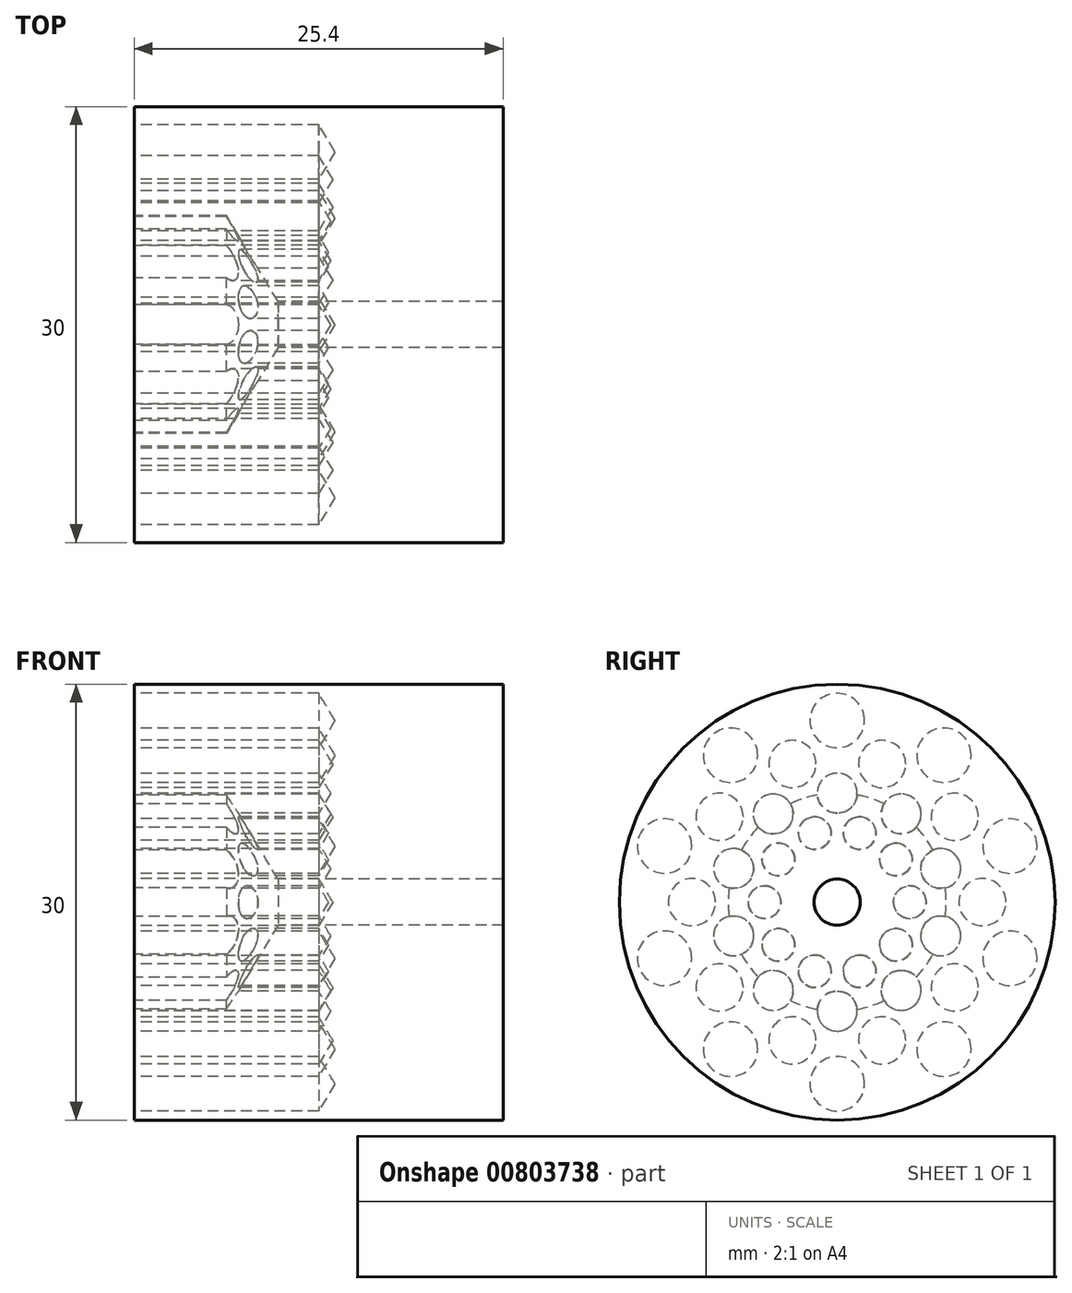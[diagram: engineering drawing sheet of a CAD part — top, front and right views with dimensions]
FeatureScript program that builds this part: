
annotation { "Feature Type Name" : "Feature", "Feature Type Description" : "" }
export const myFeature = defineFeature(function(context is Context, id is Id, definition is map)
    precondition{}
    {
        {
            var Q0;
            Q0=qCreatedBy(makeId("Right.planeOp"),FACE);
            var sketch = newSketch(context, id + "F0", { "sketchPlane" : qUnion([Q0])});
            skCircle(sketch, "E0", {"center": v(0, 0) * mm, "radius": 15 * mm});
            skCircle(sketch, "E1", {"center": v(0, 0) * mm, "radius": 1.59 * mm});
            skSolve(sketch);
        }
        {
            var Q0;
            Q0=makeQuery(id+"F0.imprint","IMPRINT",FACE,{"disambiguationData":[TD([[makeQuery(id+"F0.imprint","IMPRINT",EDGE,{"derivedFrom":sQuery(id+"F0.wireOp",EDGE,"E0")}),1.0]])]});
            extrude(context, id + "F1", {"entities" : qUnion([Q0]), "depth" : 25.4 * mm, "offsetDistance" : 25.4 * mm});
        }
        {
            var Q0;
            Q0=makeQuery(id+"F1.opExtrude","CAP_FACE",FACE,{"disambiguationData":[OSD([sQuery(id+"F0.wireOp",EDGE,"E0"),sQuery(id+"F0.wireOp",EDGE,"E1")])],"isStart":true});
            var sketch = newSketch(context, id + "F2", { "sketchPlane" : qUnion([Q0])});
            skCircle(sketch, "E2.cCircle", {"center": v(0, 0) * mm, "radius": 12.5 * mm, "construction": true});
            skLineSegment(sketch, "E2.0", {"start": v(0, 12.5) * mm, "end": v(7.35, 10.11) * mm});
            skLineSegment(sketch, "E2.1", {"start": v(7.35, 10.11) * mm, "end": v(11.89, 3.86) * mm});
            skLineSegment(sketch, "E2.2", {"start": v(11.89, 3.86) * mm, "end": v(11.89, -3.86) * mm});
            skLineSegment(sketch, "E2.3", {"start": v(11.89, -3.86) * mm, "end": v(7.35, -10.11) * mm});
            skLineSegment(sketch, "E2.4", {"start": v(7.35, -10.11) * mm, "end": v(0, -12.5) * mm});
            skLineSegment(sketch, "E2.5", {"start": v(0, -12.5) * mm, "end": v(-7.35, -10.11) * mm});
            skLineSegment(sketch, "E2.6", {"start": v(-7.35, -10.11) * mm, "end": v(-11.89, -3.86) * mm});
            skLineSegment(sketch, "E2.7", {"start": v(-11.89, -3.86) * mm, "end": v(-11.89, 3.86) * mm});
            skLineSegment(sketch, "E2.8", {"start": v(-11.89, 3.86) * mm, "end": v(-7.35, 10.11) * mm});
            skLineSegment(sketch, "E2.9", {"start": v(-7.35, 10.11) * mm, "end": v(0, 12.5) * mm});
            skCircle(sketch, "E3.cCircle", {"center": v(0, 0) * mm, "radius": 10 * mm, "construction": true});
            skLineSegment(sketch, "E3.0", {"start": v(-10, 0) * mm, "end": v(-8.1, 5.88) * mm});
            skLineSegment(sketch, "E3.1", {"start": v(-8.1, 5.88) * mm, "end": v(-3.1, 9.51) * mm});
            skLineSegment(sketch, "E3.2", {"start": v(-3.1, 9.51) * mm, "end": v(3.1, 9.51) * mm});
            skLineSegment(sketch, "E3.3", {"start": v(3.1, 9.51) * mm, "end": v(8.1, 5.88) * mm});
            skLineSegment(sketch, "E3.4", {"start": v(8.1, 5.88) * mm, "end": v(10, 0) * mm});
            skLineSegment(sketch, "E3.5", {"start": v(10, 0) * mm, "end": v(8.1, -5.88) * mm});
            skLineSegment(sketch, "E3.6", {"start": v(8.1, -5.88) * mm, "end": v(3.1, -9.51) * mm});
            skLineSegment(sketch, "E3.7", {"start": v(3.1, -9.51) * mm, "end": v(-3.1, -9.51) * mm});
            skLineSegment(sketch, "E3.8", {"start": v(-3.1, -9.51) * mm, "end": v(-8.1, -5.88) * mm});
            skLineSegment(sketch, "E3.9", {"start": v(-8.1, -5.88) * mm, "end": v(-10, 0) * mm});
            skCircle(sketch, "E4.cCircle", {"center": v(0, 0) * mm, "radius": 7.5 * mm, "construction": true});
            skLineSegment(sketch, "E4.0", {"start": v(0, 7.5) * mm, "end": v(4.4, 6.07) * mm});
            skLineSegment(sketch, "E4.1", {"start": v(4.4, 6.07) * mm, "end": v(7.13, 2.32) * mm});
            skLineSegment(sketch, "E4.2", {"start": v(7.13, 2.32) * mm, "end": v(7.13, -2.32) * mm});
            skLineSegment(sketch, "E4.3", {"start": v(7.13, -2.32) * mm, "end": v(4.4, -6.07) * mm});
            skLineSegment(sketch, "E4.4", {"start": v(4.4, -6.07) * mm, "end": v(0, -7.5) * mm});
            skLineSegment(sketch, "E4.5", {"start": v(0, -7.5) * mm, "end": v(-4.4, -6.07) * mm});
            skLineSegment(sketch, "E4.6", {"start": v(-4.4, -6.07) * mm, "end": v(-7.13, -2.32) * mm});
            skLineSegment(sketch, "E4.7", {"start": v(-7.13, -2.32) * mm, "end": v(-7.13, 2.32) * mm});
            skLineSegment(sketch, "E4.8", {"start": v(-7.13, 2.32) * mm, "end": v(-4.4, 6.07) * mm});
            skLineSegment(sketch, "E4.9", {"start": v(-4.4, 6.07) * mm, "end": v(0, 7.5) * mm});
            skCircle(sketch, "E5.cCircle", {"center": v(0, 0) * mm, "radius": 5 * mm, "construction": true});
            skLineSegment(sketch, "E5.0", {"start": v(-5, 0) * mm, "end": v(-4.05, 2.94) * mm});
            skLineSegment(sketch, "E5.1", {"start": v(-4.05, 2.94) * mm, "end": v(-1.55, 4.76) * mm});
            skLineSegment(sketch, "E5.2", {"start": v(-1.55, 4.76) * mm, "end": v(1.55, 4.76) * mm});
            skLineSegment(sketch, "E5.3", {"start": v(1.55, 4.76) * mm, "end": v(4.05, 2.94) * mm});
            skLineSegment(sketch, "E5.4", {"start": v(4.05, 2.94) * mm, "end": v(5, 0) * mm});
            skLineSegment(sketch, "E5.5", {"start": v(5, 0) * mm, "end": v(4.05, -2.94) * mm});
            skLineSegment(sketch, "E5.6", {"start": v(4.05, -2.94) * mm, "end": v(1.55, -4.76) * mm});
            skLineSegment(sketch, "E5.7", {"start": v(1.55, -4.76) * mm, "end": v(-1.55, -4.76) * mm});
            skLineSegment(sketch, "E5.8", {"start": v(-1.55, -4.76) * mm, "end": v(-4.05, -2.94) * mm});
            skLineSegment(sketch, "E5.9", {"start": v(-4.05, -2.94) * mm, "end": v(-5, 0) * mm});
            skSolve(sketch);
        }
        {
            var Q0;
            Q0=sQuery(id+"F2.wireOp",VERTEX,"E2.7.end");
            var Q1;
            Q1=sQuery(id+"F2.wireOp",VERTEX,"E2.8.end");
            var Q2;
            Q2=sQuery(id+"F2.wireOp",VERTEX,"E2.0.start");
            var Q3;
            Q3=sQuery(id+"F2.wireOp",VERTEX,"E2.0.end");
            var Q4;
            Q4=sQuery(id+"F2.wireOp",VERTEX,"E2.1.end");
            var Q5;
            Q5=sQuery(id+"F2.wireOp",VERTEX,"E2.2.end");
            var Q6;
            Q6=sQuery(id+"F2.wireOp",VERTEX,"E2.3.end");
            var Q7;
            Q7=sQuery(id+"F2.wireOp",VERTEX,"E2.4.end");
            var Q8;
            Q8=sQuery(id+"F2.wireOp",VERTEX,"E2.5.end");
            var Q9;
            Q9=sQuery(id+"F2.wireOp",VERTEX,"E2.6.end");
            var Q10;
            Q10=makeQuery(id+"F1.opExtrude","SWEPT_BODY",BODY,{"disambiguationData":[OSD([sQuery(id+"F0.wireOp",EDGE,"E0"),sQuery(id+"F0.wireOp",EDGE,"E1")])]});
            hole(context, id + "F3", {"style" : HoleStyle.SIMPLE, "endStyle" : HoleEndStyle.BLIND, "holeDiameter" : 3.75 * mm, "majorDiameter" : 6.35 * mm, "holeDepth" : 12.7 * mm, "isTappedThrough" : true, "tappedDepth" : 12.7 * mm, "tapClearance" : 3, "locations" : qUnion([Q0, Q1, Q2, Q3, Q4, Q5, Q6, Q7, Q8, Q9]), "scope" : qUnion([Q10])});
        }
        {
            var Q0;
            Q0=sQuery(id+"F2.wireOp",VERTEX,"E3.8.end");
            var Q1;
            Q1=sQuery(id+"F2.wireOp",VERTEX,"E3.0.start");
            var Q2;
            Q2=sQuery(id+"F2.wireOp",VERTEX,"E3.0.end");
            var Q3;
            Q3=sQuery(id+"F2.wireOp",VERTEX,"E3.1.end");
            var Q4;
            Q4=sQuery(id+"F2.wireOp",VERTEX,"E3.2.end");
            var Q5;
            Q5=sQuery(id+"F2.wireOp",VERTEX,"E3.3.end");
            var Q6;
            Q6=sQuery(id+"F2.wireOp",VERTEX,"E3.4.end");
            var Q7;
            Q7=sQuery(id+"F2.wireOp",VERTEX,"E3.5.end");
            var Q8;
            Q8=sQuery(id+"F2.wireOp",VERTEX,"E3.6.end");
            var Q9;
            Q9=sQuery(id+"F2.wireOp",VERTEX,"E3.7.end");
            var Q10;
            Q10=makeQuery(id+"F1.opExtrude","SWEPT_BODY",BODY,{"disambiguationData":[OSD([sQuery(id+"F0.wireOp",EDGE,"E0"),sQuery(id+"F0.wireOp",EDGE,"E1")])]});
            hole(context, id + "F4", {"style" : HoleStyle.SIMPLE, "endStyle" : HoleEndStyle.BLIND, "holeDiameter" : 3.25 * mm, "majorDiameter" : 6.35 * mm, "holeDepth" : 12.7 * mm, "isTappedThrough" : true, "tappedDepth" : 12.7 * mm, "tapClearance" : 3, "locations" : qUnion([Q0, Q1, Q2, Q3, Q4, Q5, Q6, Q7, Q8, Q9]), "scope" : qUnion([Q10])});
        }
        {
            var Q0;
            Q0=sQuery(id+"F2.wireOp",VERTEX,"E4.6.end");
            var Q1;
            Q1=sQuery(id+"F2.wireOp",VERTEX,"E4.7.end");
            var Q2;
            Q2=sQuery(id+"F2.wireOp",VERTEX,"E4.8.end");
            var Q3;
            Q3=sQuery(id+"F2.wireOp",VERTEX,"E4.0.start");
            var Q4;
            Q4=sQuery(id+"F2.wireOp",VERTEX,"E4.0.end");
            var Q5;
            Q5=sQuery(id+"F2.wireOp",VERTEX,"E4.1.end");
            var Q6;
            Q6=sQuery(id+"F2.wireOp",VERTEX,"E4.2.end");
            var Q7;
            Q7=sQuery(id+"F2.wireOp",VERTEX,"E4.3.end");
            var Q8;
            Q8=sQuery(id+"F2.wireOp",VERTEX,"E4.4.end");
            var Q9;
            Q9=sQuery(id+"F2.wireOp",VERTEX,"E4.5.end");
            var Q10;
            Q10=makeQuery(id+"F1.opExtrude","SWEPT_BODY",BODY,{"disambiguationData":[OSD([sQuery(id+"F0.wireOp",EDGE,"E0"),sQuery(id+"F0.wireOp",EDGE,"E1")])]});
            hole(context, id + "F5", {"style" : HoleStyle.SIMPLE, "endStyle" : HoleEndStyle.BLIND, "holeDiameter" : 2.75 * mm, "majorDiameter" : 6.35 * mm, "holeDepth" : 12.7 * mm, "isTappedThrough" : true, "tappedDepth" : 12.7 * mm, "tapClearance" : 3, "locations" : qUnion([Q0, Q1, Q2, Q3, Q4, Q5, Q6, Q7, Q8, Q9]), "scope" : qUnion([Q10])});
        }
        {
            var Q0;
            Q0=sQuery(id+"F2.wireOp",VERTEX,"E5.8.end");
            var Q1;
            Q1=sQuery(id+"F2.wireOp",VERTEX,"E5.0.start");
            var Q2;
            Q2=sQuery(id+"F2.wireOp",VERTEX,"E5.0.end");
            var Q3;
            Q3=sQuery(id+"F2.wireOp",VERTEX,"E5.1.end");
            var Q4;
            Q4=sQuery(id+"F2.wireOp",VERTEX,"E5.2.end");
            var Q5;
            Q5=sQuery(id+"F2.wireOp",VERTEX,"E5.3.end");
            var Q6;
            Q6=sQuery(id+"F2.wireOp",VERTEX,"E5.4.end");
            var Q7;
            Q7=sQuery(id+"F2.wireOp",VERTEX,"E5.5.end");
            var Q8;
            Q8=sQuery(id+"F2.wireOp",VERTEX,"E5.6.end");
            var Q9;
            Q9=sQuery(id+"F2.wireOp",VERTEX,"E5.7.end");
            var Q10;
            Q10=makeQuery(id+"F1.opExtrude","SWEPT_BODY",BODY,{"disambiguationData":[OSD([sQuery(id+"F0.wireOp",EDGE,"E0"),sQuery(id+"F0.wireOp",EDGE,"E1")])]});
            hole(context, id + "F6", {"style" : HoleStyle.SIMPLE, "endStyle" : HoleEndStyle.BLIND, "holeDiameter" : 2.25 * mm, "majorDiameter" : 6.35 * mm, "holeDepth" : 12.7 * mm, "isTappedThrough" : true, "tappedDepth" : 12.7 * mm, "tapClearance" : 3, "locations" : qUnion([Q0, Q1, Q2, Q3, Q4, Q5, Q6, Q7, Q8, Q9]), "scope" : qUnion([Q10])});
        }
        {
            var Q0;
            Q0=sQuery(id+"F0.wireOp",VERTEX,"E0.center");
            var Q1;
            Q1=makeQuery(id+"F1.opExtrude","SWEPT_BODY",BODY,{"disambiguationData":[OSD([sQuery(id+"F0.wireOp",EDGE,"E0"),sQuery(id+"F0.wireOp",EDGE,"E1")])]});
            hole(context, id + "F7", {"style" : HoleStyle.SIMPLE, "endStyle" : HoleEndStyle.BLIND, "oppositeDirection" : true, "holeDiameter" : 15 * mm, "majorDiameter" : 6.35 * mm, "holeDepth" : 6.35 * mm, "isTappedThrough" : true, "tappedDepth" : 12.7 * mm, "tapClearance" : 3, "startFromSketch" : true, "locations" : qUnion([Q0]), "scope" : qUnion([Q1])});
        }
    });
